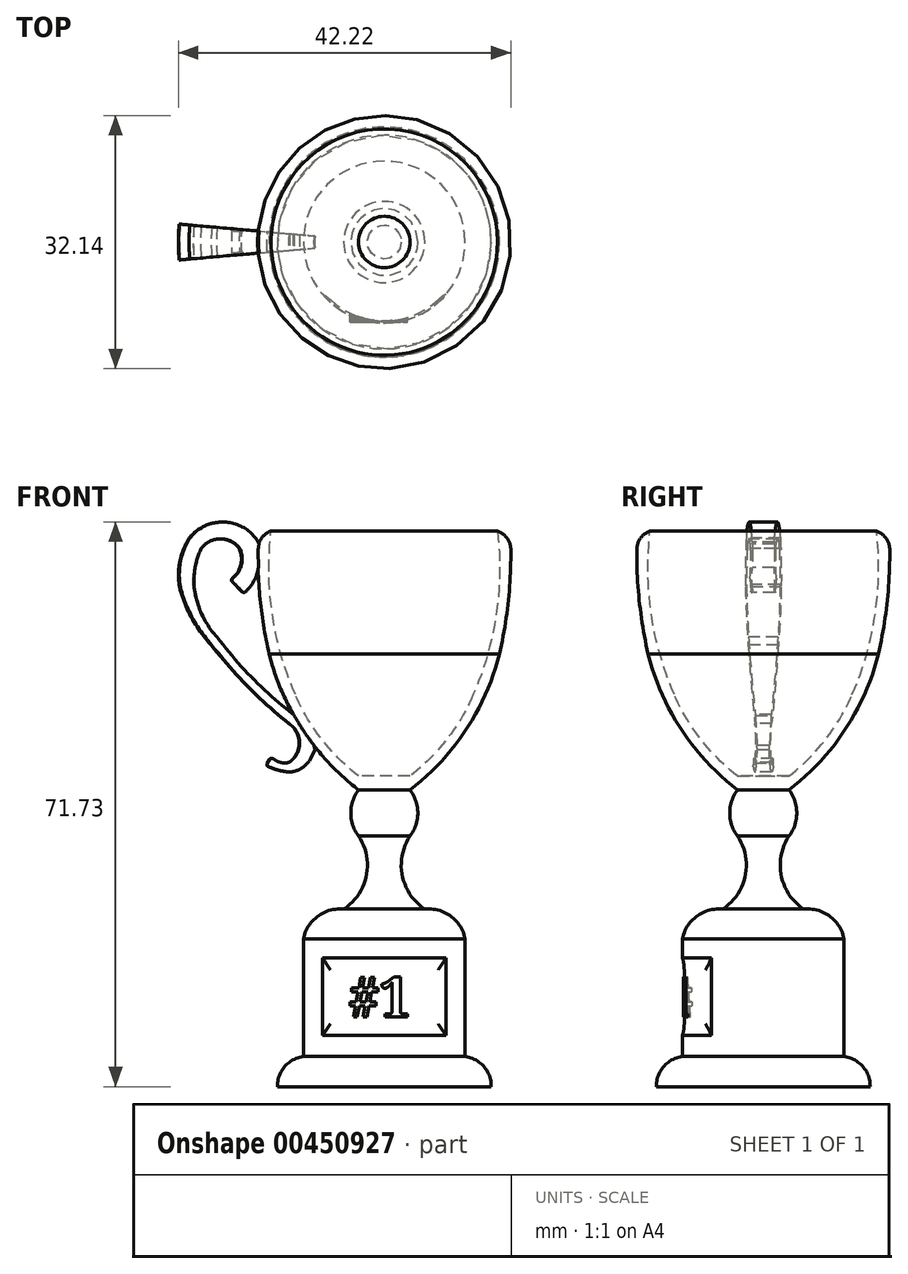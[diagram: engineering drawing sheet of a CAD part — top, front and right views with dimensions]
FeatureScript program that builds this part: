
annotation { "Feature Type Name" : "Feature", "Feature Type Description" : "" }
export const myFeature = defineFeature(function(context is Context, id is Id, definition is map)
    precondition{}
    {
        {
            var Q0;
            Q0=qCreatedBy(makeId("Front.planeOp"),FACE);
            var sketch = newSketch(context, id + "F0", { "sketchPlane" : qUnion([Q0])});
            skArc(sketch, "E0", {"start": v(-16, 36.3) * mm, "mid": v(-15.85, 28.37) * mm, "end": v(-14.63, 20.54) * mm});
            skArc(sketch, "E1", {"start": v(-14.63, 20.54) * mm, "mid": v(-10.4, 10.97) * mm, "end": v(-3.26, 3.3) * mm});
            skArc(sketch, "E2", {"start": v(-3.26, 3.3) * mm, "mid": v(-4.26, 0.37) * mm, "end": v(-3.26, -2.57) * mm});
            skArc(sketch, "E3", {"start": v(-5.16, -11.85) * mm, "mid": v(-2.29, -7.6) * mm, "end": v(-3.26, -2.57) * mm});
            skArc(sketch, "E4", {"start": v(-5.16, -11.85) * mm, "mid": v(-8.46, -12.75) * mm, "end": v(-10.27, -15.64) * mm});
            skLineSegment(sketch, "E5", {"start": v(-10.27, -15.64) * mm, "end": v(-10.27, -30.57) * mm});
            skLineSegment(sketch, "E6", {"start": v(0, -34.4) * mm, "end": v(-13.58, -34.4) * mm});
            skArc(sketch, "E7", {"start": v(-10.27, -30.57) * mm, "mid": v(-12.66, -31.85) * mm, "end": v(-13.58, -34.4) * mm});
            skArc(sketch, "E8", {"start": v(-11.3, 15.41) * mm, "mid": v(-7.94, 9.73) * mm, "end": v(-3.26, 5.06) * mm});
            skArc(sketch, "E9", {"start": v(-14.38, 36.2) * mm, "mid": v(-14.22, 25.6) * mm, "end": v(-11.3, 15.41) * mm});
            skLineSegment(sketch, "E10", {"start": v(-16, 36.3) * mm, "end": v(-14.38, 36.2) * mm});
            skLineSegment(sketch, "E11", {"start": v(-3.26, 5.06) * mm, "end": v(0, 5.06) * mm});
            skLineSegment(sketch, "E12", {"start": v(0, 5.06) * mm, "end": v(0, -34.4) * mm});
            skSolve(sketch);
        }
        {
            var Q0;
            Q0=qSketchRegion(id+"F0",true);
            var Q1;
            Q1=sQuery(id+"F0.wireOp",EDGE,"E12");
            revolve(context, id + "F1", {"entities" : qUnion([Q0]), "axis" : qUnion([Q1]), "revolveType" : RevolveType.FULL});
        }
        {
            var Q0;
            Q0=qCreatedBy(makeId("Front.planeOp"),FACE);
            var sketch = newSketch(context, id + "F2", { "sketchPlane" : qUnion([Q0])});
            skArc(sketch, "E13", {"start": v(-16.08, 34.82) * mm, "mid": v(-20.32, 37.32) * mm, "end": v(-24.8, 35.27) * mm});
            skArc(sketch, "E14", {"start": v(-24.8, 35.27) * mm, "mid": v(-25.99, 32.28) * mm, "end": v(-26, 29.06) * mm});
            skArc(sketch, "E15", {"start": v(-26, 29.06) * mm, "mid": v(-24.46, 25.14) * mm, "end": v(-22, 21.71) * mm});
            skArc(sketch, "E16", {"start": v(-22, 21.71) * mm, "mid": v(-17.35, 16.43) * mm, "end": v(-12.14, 11.7) * mm});
            skArc(sketch, "E17", {"start": v(-12.14, 6.78) * mm, "mid": v(-10.8, 9.25) * mm, "end": v(-12.14, 11.7) * mm});
            skArc(sketch, "E18", {"start": v(-14.42, 7.47) * mm, "mid": v(-13.37, 6.83) * mm, "end": v(-12.14, 6.78) * mm});
            skLineSegment(sketch, "E19", {"start": v(-14.42, 7.47) * mm, "end": v(-15.02, 6.4) * mm});
            skArc(sketch, "E20", {"start": v(-15.02, 6.4) * mm, "mid": v(-13.59, 5.83) * mm, "end": v(-12.07, 5.57) * mm});
            skArc(sketch, "E21", {"start": v(-12.07, 5.57) * mm, "mid": v(-10.46, 6.12) * mm, "end": v(-9.34, 7.4) * mm});
            skLineSegment(sketch, "E22", {"start": v(-9.34, 7.4) * mm, "end": v(-8.84, 8.4) * mm});
            skLineSegment(sketch, "E23", {"start": v(-8.84, 8.4) * mm, "end": v(-9.04, 9.37) * mm});
            skLineSegment(sketch, "E24", {"start": v(-9.04, 9.37) * mm, "end": v(-11.6, 12.9) * mm});
            skArc(sketch, "E25", {"start": v(-21.31, 22.7) * mm, "mid": v(-16.78, 17.47) * mm, "end": v(-11.6, 12.9) * mm});
            skArc(sketch, "E26", {"start": v(-24.27, 29.36) * mm, "mid": v(-23.34, 25.78) * mm, "end": v(-21.31, 22.7) * mm});
            skArc(sketch, "E27", {"start": v(-23.34, 33.99) * mm, "mid": v(-24.08, 31.73) * mm, "end": v(-24.27, 29.36) * mm});
            skPoint(sketch, "E27.startSnap0", {"position": v(-23.34, 25.78) * mm});
            skArc(sketch, "E28", {"start": v(-18.43, 33.99) * mm, "mid": v(-20.89, 35.2) * mm, "end": v(-23.34, 33.99) * mm});
            skArc(sketch, "E29", {"start": v(-19.57, 29.97) * mm, "mid": v(-18.25, 31.77) * mm, "end": v(-18.43, 33.99) * mm});
            skLineSegment(sketch, "E30", {"start": v(-19.57, 29.97) * mm, "end": v(-17.9, 28.3) * mm});
            skArc(sketch, "E31", {"start": v(-17.9, 28.3) * mm, "mid": v(-16.6, 29.9) * mm, "end": v(-16, 31.86) * mm});
            skArc(sketch, "E32", {"start": v(-16, 31.86) * mm, "mid": v(-15.76, 33.35) * mm, "end": v(-16.08, 34.82) * mm});
            skSolve(sketch);
        }
        {
            var Q0;
            Q0=makeQuery(id+"F2.imprint","IMPRINT",FACE,{"disambiguationData":[TD([[makeQuery(id+"F2.imprint","IMPRINT",EDGE,{"derivedFrom":sQuery(id+"F2.wireOp",EDGE,"E13")}),1.0]])]});
            var Q1;
            Q1=sQuery(id+"F0.wireOp",EDGE,"E12");
            revolve(context, id + "F3", {"operationType" : NewBodyOperationType.ADD, "entities" : qUnion([Q0]), "axis" : qUnion([Q1]), "revolveType" : RevolveType.TWO_DIRECTIONS, "angle" : 5 * degree, "angleBack" : 355 * degree});
        }
        {
            var Q0;
            Q0=makeQuery(id+"F1.opRevolve","SWEPT_EDGE",EDGE,{"disambiguationData":[OSD([sQuery(id+"F0.wireOp",EDGE,"E0"),sQuery(id+"F0.wireOp",EDGE,"E10")])]});
            fillet(context, id + "F4", {"entities" : qUnion([Q0]), "radius" : 2.54 * mm, "tangentPropagation" : true, "allowEdgeOverflow" : false});
        }
        {
            var Q0;
            Q0=makeQuery(id+"F3.opRevolve","SWEPT_EDGE",EDGE,{"disambiguationData":[OSD([sQuery(id+"F2.wireOp",EDGE,"E18"),sQuery(id+"F2.wireOp",EDGE,"E19")])]});
            var Q1;
            Q1=makeQuery(id+"F3.opRevolve","SWEPT_EDGE",EDGE,{"disambiguationData":[OSD([sQuery(id+"F2.wireOp",EDGE,"E19"),sQuery(id+"F2.wireOp",EDGE,"E20")])]});
            var Q2;
            Q2=makeQuery(id+"FtzzwsuBMxib6I8_1.1.F3.opRevolve","SWEPT_EDGE",EDGE,{"disambiguationData":[OSD([sQuery(id+"F2.wireOp",EDGE,"E18"),sQuery(id+"F2.wireOp",EDGE,"E19")])]});
            var Q3;
            Q3=makeQuery(id+"FtzzwsuBMxib6I8_1.1.F3.opRevolve","SWEPT_EDGE",EDGE,{"disambiguationData":[OSD([sQuery(id+"F2.wireOp",EDGE,"E19"),sQuery(id+"F2.wireOp",EDGE,"E20")])]});
            var Q4;
            Q4=makeQuery(id+"FtzzwsuBMxib6I8_1.1.F3.opRevolve","SWEPT_EDGE",EDGE,{"disambiguationData":[OSD([sQuery(id+"F2.wireOp",EDGE,"E29"),sQuery(id+"F2.wireOp",EDGE,"E30")])]});
            var Q5;
            Q5=makeQuery(id+"FtzzwsuBMxib6I8_1.1.F3.opRevolve","SWEPT_EDGE",EDGE,{"disambiguationData":[OSD([sQuery(id+"F2.wireOp",EDGE,"E30"),sQuery(id+"F2.wireOp",EDGE,"E31")])]});
            var Q6;
            Q6=makeQuery(id+"F3.opRevolve","SWEPT_EDGE",EDGE,{"disambiguationData":[OSD([sQuery(id+"F2.wireOp",EDGE,"E30"),sQuery(id+"F2.wireOp",EDGE,"E31")])]});
            var Q7;
            Q7=makeQuery(id+"F3.opRevolve","SWEPT_EDGE",EDGE,{"disambiguationData":[OSD([sQuery(id+"F2.wireOp",EDGE,"E29"),sQuery(id+"F2.wireOp",EDGE,"E30")])]});
            var Q8;
            Q8=makeQuery(id+"F3.opRevolve","CAP_EDGE",EDGE,{"disambiguationData":[OSD([sQuery(id+"F2.wireOp",EDGE,"E30")])],"isStart":false});
            var Q9;
            Q9=makeQuery(id+"F3.opRevolve","CAP_EDGE",EDGE,{"disambiguationData":[OSD([sQuery(id+"F2.wireOp",EDGE,"E30")])],"isStart":true});
            var Q10;
            Q10=makeQuery(id+"F3.opRevolve","CAP_EDGE",EDGE,{"disambiguationData":[OSD([sQuery(id+"F2.wireOp",EDGE,"E19")])],"isStart":false});
            var Q11;
            Q11=makeQuery(id+"F3.opRevolve","CAP_EDGE",EDGE,{"disambiguationData":[OSD([sQuery(id+"F2.wireOp",EDGE,"E19")])],"isStart":true});
            var Q12;
            Q12=makeQuery(id+"FtzzwsuBMxib6I8_1.1.F3.opRevolve","CAP_EDGE",EDGE,{"disambiguationData":[OSD([sQuery(id+"F2.wireOp",EDGE,"E19")])],"isStart":false});
            var Q13;
            Q13=makeQuery(id+"FtzzwsuBMxib6I8_1.1.F3.opRevolve","CAP_EDGE",EDGE,{"disambiguationData":[OSD([sQuery(id+"F2.wireOp",EDGE,"E19")])],"isStart":true});
            var Q14;
            Q14=makeQuery(id+"FtzzwsuBMxib6I8_1.1.F3.opRevolve","CAP_EDGE",EDGE,{"disambiguationData":[OSD([sQuery(id+"F2.wireOp",EDGE,"E30")])],"isStart":false});
            var Q15;
            Q15=makeQuery(id+"FtzzwsuBMxib6I8_1.1.F3.opRevolve","CAP_EDGE",EDGE,{"disambiguationData":[OSD([sQuery(id+"F2.wireOp",EDGE,"E30")])],"isStart":true});
            fillet(context, id + "F5", {"entities" : qUnion([Q0, Q1, Q2, Q3, Q4, Q5, Q6, Q7, Q8, Q9, Q10, Q11, Q12, Q13, Q14, Q15]), "radius" : 0.25 * mm, "tangentPropagation" : true, "allowEdgeOverflow" : false});
        }
        {
            var Q0;
            Q0=qCreatedBy(makeId("Right.planeOp"),FACE);
            var sketch = newSketch(context, id + "F6", { "sketchPlane" : qUnion([Q0])});
            skLineSegment(sketch, "E33.bottom", {"start": v(-10.6, -18.06) * mm, "end": v(-10.04, -18.06) * mm});
            skLineSegment(sketch, "E33.top", {"start": v(-10.6, -27.91) * mm, "end": v(-10.04, -27.91) * mm});
            skLineSegment(sketch, "E33.left", {"start": v(-10.6, -18.06) * mm, "end": v(-10.6, -27.91) * mm});
            skLineSegment(sketch, "E33.right", {"start": v(-10.04, -18.06) * mm, "end": v(-10.04, -27.91) * mm});
            skSolve(sketch);
        }
        {
            var Q0;
            Q0=qSketchRegion(id+"F6",true);
            var Q1;
            Q1=sQuery(id+"F0.wireOp",EDGE,"E12");
            revolve(context, id + "F7", {"operationType" : NewBodyOperationType.REMOVE, "entities" : qUnion([Q0]), "axis" : qUnion([Q1]), "revolveType" : RevolveType.SYMMETRIC, "oppositeDirection" : true, "angle" : 100 * degree});
        }
        {
            var Q0;
            Q0=makeQuery(id+"F7.boolean.opBoolean","COPY",EDGE,{"derivedFrom":makeQuery(id+"F7.opRevolve","SWEPT_EDGE",EDGE,{"disambiguationData":[OSD([sQuery(id+"F6.wireOp",EDGE,"E33.bottom"),sQuery(id+"F6.wireOp",EDGE,"E33.right")])]})});
            var Q1;
            Q1=makeQuery(id+"F7.boolean.opBoolean","COPY",EDGE,{"derivedFrom":makeQuery(id+"F7.opRevolve","CAP_EDGE",EDGE,{"disambiguationData":[OSD([sQuery(id+"F6.wireOp",EDGE,"E33.right")])],"isStart":true})});
            var Q2;
            Q2=makeQuery(id+"F7.boolean.opBoolean","COPY",EDGE,{"derivedFrom":makeQuery(id+"F7.opRevolve","CAP_EDGE",EDGE,{"disambiguationData":[OSD([sQuery(id+"F6.wireOp",EDGE,"E33.right")])],"isStart":false})});
            var Q3;
            Q3=makeQuery(id+"F7.boolean.opBoolean","COPY",EDGE,{"derivedFrom":makeQuery(id+"F7.opRevolve","SWEPT_EDGE",EDGE,{"disambiguationData":[OSD([sQuery(id+"F6.wireOp",EDGE,"E33.top"),sQuery(id+"F6.wireOp",EDGE,"E33.right")])]})});
            fillet(context, id + "F8", {"entities" : qUnion([Q0, Q1, Q2, Q3]), "radius" : 5.08 * mm, "tangentPropagation" : true, "allowEdgeOverflow" : false});
        }
        {
            var Q0;
            Q0=qCreatedBy(makeId("Front.planeOp"),FACE);
            var sketch = newSketch(context, id + "F9", { "sketchPlane" : qUnion([Q0])});
            skText(sketch, "E34", { "text": "#1", "fontName": "NotoSerif-Bold.ttf"});
            const initialGuessF9  = {"E34": [-0.00457, -0.02554, 1, 0, 0.00508]};
            skSetInitialGuess(sketch, initialGuessF9);
            skSolve(sketch);
        }
        {
            var Q0;
            Q0=qSketchRegion(id+"F9",true);
            extrude(context, id + "F10", {"entities" : qUnion([Q0]), "operationType" : NewBodyOperationType.ADD, "depth" : 10.16 * mm});
        }
    });
